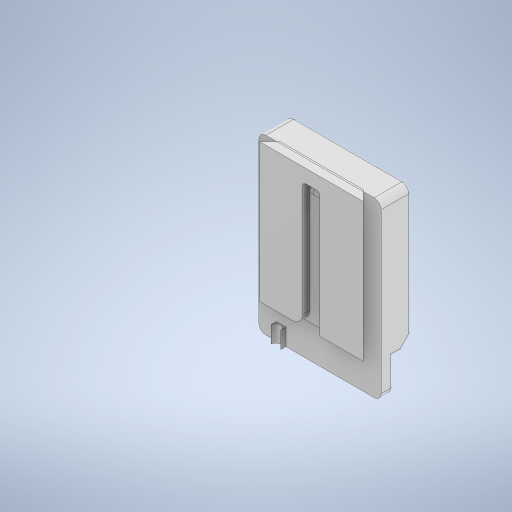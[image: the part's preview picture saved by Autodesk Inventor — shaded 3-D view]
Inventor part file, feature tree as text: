
AUTODESK INVENTOR PART (.ipt)
format: ipt  version: 2024 (Build 280153000, 153)  size: 512,512 bytes
history: native  units: mm
features: fillet x4, extrude x3, sketch x3, other x2
ambient origin geometry x8: Origin, YZ Plane, XZ Plane, XY Plane, X Axis, Y Axis, Z Axis, Center Point
bodies: Body1 (feature_tree)
feature tree (12):
  other  "Bryła1"
  extrude  "Wyciągnięcie proste1"  Depth=10.0mm
  fillet  "Zaokrąglenie1"  Radius=5.0mm
  extrude  "Wyciągnięcie proste6"  Depth=17.0mm
  extrude  "Wyciągnięcie proste7"  Depth=72.0mm
  fillet  "Zaokrąglenie2"  Radius=4.0mm
  fillet  "Zaokrąglenie3"  Radius=4.0mm
  fillet  "Zaokrąglenie4"  Radius=5.6mm
  sketch  "Szkic1"
  sketch  "Szkic5"
  sketch  "Szkic6"
  other  "Baza1"
